# Revit family: Hose_Box-Bradley_Corp-7910-Single_Valve_Recessed
name_source: partatom
category: Plumbing Fixtures
units: mm (PartAtom-declared; Revit-internal decimal feet)

## family parameters
Cut with Voids When Loaded = No
Host = Face
Part Type = Normal
Room Calculation Point = No
Round Connector Dimension = Use Diameter
Shared = No

## types (1)
- 7910
    ADA Compliant = No
    Assembly Code = D2010
    Buy American Act = To Be Determined
    Cold Water Connection Diameter = 1"
    Cold Water Connection Radius = 0"
    Default Elevation = 48 "
    Depth = 4 "
    Description = Single Valve Recessed Hose Box
    Installation Type = Wall Mounted-Recessed
    Length = 12.625 "
    Low Emitting Material = No
    Manufacturer = Bradley Corporation
    Manufacturer Installation URL - English = https://www.bradleycorp.com
    MasterFormat Number = 22 42 00
    MasterFormat Title = Commercial Plumbing Fixtures
    Material = Stainless Steel
    Model = 7910
    OmniClass Code = 23 31 00 00
    OmniClass Title = Plumbing Specific Products and Equipment
    Percentage of Recycled Content = 0
    Product Page URL = https://www.bradleycorp.com
    Product Tech Data URL - English = https://www.bradleycorp.com
    Type Comments = Single Valve Recessed Hose Box
    URL = http://www.bradleycorp.com
    Version = 1.0
    Warranty Information = Full, One-Year
    Width = 10 "

## geometry (parser evidence)
native form markers: Sweep x3
no freeform markers — native parametric forms only
